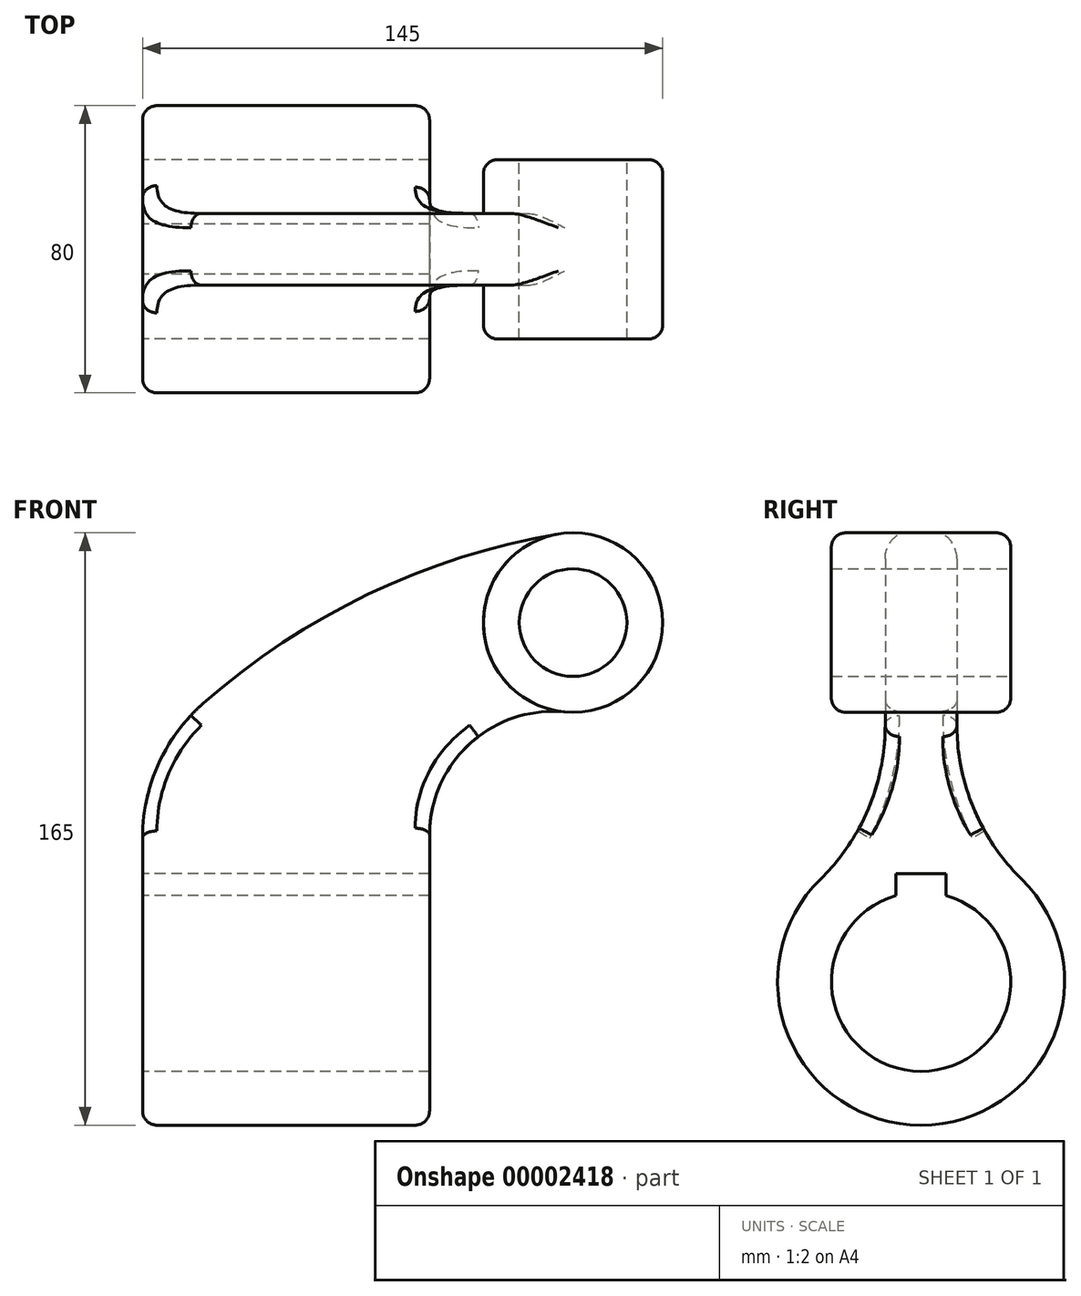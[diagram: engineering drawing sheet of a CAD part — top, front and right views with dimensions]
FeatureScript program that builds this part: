
annotation { "Feature Type Name" : "Feature", "Feature Type Description" : "" }
export const myFeature = defineFeature(function(context is Context, id is Id, definition is map)
    precondition{}
    {
        {
            var Q0;
            Q0=qCreatedBy(makeId("Front.planeOp"),FACE);
            var sketch = newSketch(context, id + "F0", { "sketchPlane" : qUnion([Q0])});
            skLineSegment(sketch, "E0", {"start": v(0, 0) * mm, "end": v(80, 0) * mm});
            skLineSegment(sketch, "E1", {"start": v(80, 0) * mm, "end": v(80, 40.8) * mm});
            skLineSegment(sketch, "E2", {"start": v(0, 0) * mm, "end": v(0, 40) * mm});
            skArc(sketch, "E3", {"start": v(0, 40) * mm, "mid": v(4.43, 60.58) * mm, "end": v(16.95, 77.52) * mm});
            skArc(sketch, "E4", {"start": v(16.95, 77.52) * mm, "mid": v(63.1, 107.99) * mm, "end": v(115.84, 124.65) * mm});
            skCircle(sketch, "E5", {"center": v(120, 100) * mm, "radius": 25 * mm});
            skArc(sketch, "E6", {"start": v(80, 40.8) * mm, "mid": v(91.26, 66.28) * mm, "end": v(117.67, 75.1) * mm});
            skCircle(sketch, "E7", {"center": v(120, 100) * mm, "radius": 15 * mm});
            skSolve(sketch);
        }
        {
            var Q0;
            Q0=qCreatedBy(makeId("Right.planeOp"),FACE);
            var sketch = newSketch(context, id + "F1", { "sketchPlane" : qUnion([Q0])});
            skCircle(sketch, "E8", {"center": v(0, 0) * mm, "radius": 40 * mm});
            skArc(sketch, "E9", {"start": v(-7, 24) * mm, "mid": v(0, -25) * mm, "end": v(7, 24) * mm});
            skLineSegment(sketch, "E10", {"start": v(0, 0) * mm, "end": v(0, -60.12) * mm, "construction": true});
            skLineSegment(sketch, "E11", {"start": v(0, 30) * mm, "end": v(7, 30) * mm});
            skLineSegment(sketch, "E12", {"start": v(7, 30) * mm, "end": v(7, 24) * mm});
            skLineSegment(sketch, "E13.0.MirrorCS", {"start": v(-7, 30) * mm, "end": v(-7, 24) * mm});
            skLineSegment(sketch, "E13.1.MirrorCS", {"start": v(0, 30) * mm, "end": v(-7, 30) * mm});
            skSolve(sketch);
        }
        {
            var Q0;
            Q0=makeQuery(id+"F1.imprint","IMPRINT",FACE,{"disambiguationData":[TD([[makeQuery(id+"F1.imprint","IMPRINT",EDGE,{"derivedFrom":sQuery(id+"F1.wireOp",EDGE,"E8")}),1.0]])]});
            var Q1;
            Q1=makeQuery(id+"F1.imprint","IMPRINT",FACE,{"disambiguationData":[TD([[makeQuery(id+"F1.imprint","IMPRINT",EDGE,{"derivedFrom":sQuery(id+"F1.wireOp",EDGE,"E9")}),1.0]])]});
            var Q2;
            Q2=sQuery(id+"F1.wireOp",EDGE,"E8");
            extrude(context, id + "F2", {"entities" : qUnion([Q0, Q1]), "surfaceEntities" : qUnion([Q2]), "depth" : 80 * mm});
        }
        {
            var Q0;
            Q0=makeQuery(id+"F0.imprint","IMPRINT",FACE,{"disambiguationData":[TD([[makeQuery(id+"F0.imprint","IMPRINT",EDGE,{"derivedFrom":sQuery(id+"F0.wireOp",EDGE,"E7")}),-1.0]])]});
            extrude(context, id + "F3", {"entities" : qUnion([Q0]), "endBound" : BoundingType.SYMMETRIC, "depth" : 50 * mm});
        }
        {
            var Q0;
            Q0=makeQuery(id+"F0.imprint","IMPRINT",FACE,{"disambiguationData":[TD([[makeQuery(id+"F0.imprint","IMPRINT",EDGE,{"derivedFrom":sQuery(id+"F0.wireOp",EDGE,"E0")}),1.0]])]});
            extrude(context, id + "F4", {"entities" : qUnion([Q0]), "endBound" : BoundingType.SYMMETRIC, "depth" : 20 * mm});
        }
        {
            var Q0;
            Q0=makeQuery(id+"F4.opExtrude","SWEPT_BODY",BODY,{"disambiguationData":[OSD([sQuery(id+"F0.wireOp",EDGE,"E0"),sQuery(id+"F0.wireOp",EDGE,"E1"),sQuery(id+"F0.wireOp",EDGE,"E2"),sQuery(id+"F0.wireOp",EDGE,"E3"),sQuery(id+"F0.wireOp",EDGE,"E4"),sQuery(id+"F0.wireOp",EDGE,"E5"),sQuery(id+"F0.wireOp",EDGE,"E6")])]});
            var Q1;
            Q1=makeQuery(id+"F2.opExtrude","SWEPT_BODY",BODY,{"disambiguationData":[OSD([sQuery(id+"F1.wireOp",EDGE,"E8")])]});
            var Q2;
            Q2=makeQuery(id+"F3.opExtrude","SWEPT_BODY",BODY,{"disambiguationData":[OSD([sQuery(id+"F0.wireOp",EDGE,"E5"),sQuery(id+"F0.wireOp",EDGE,"E7")])]});
            booleanBodies(context, id + "F5", {"operationType" : BooleanOperationType.UNION, "tools" : qUnion([Q0, Q1, Q2])});
        }
        {
            var Q0;
            Q0=makeQuery(id+"F1.imprint","IMPRINT",FACE,{"disambiguationData":[TD([[makeQuery(id+"F1.imprint","IMPRINT",EDGE,{"derivedFrom":sQuery(id+"F1.wireOp",EDGE,"E9")}),1.0]])]});
            extrude(context, id + "F6", {"entities" : qUnion([Q0]), "operationType" : NewBodyOperationType.REMOVE, "endBound" : BoundingType.THROUGH_ALL, "depth" : 25 * mm});
        }
        {
            var Q0;
            Q0=makeQuery(id+"F5.opBoolean","INTERSECT",EDGE,{"derivedFrom":[makeQuery(id+"F2.opExtrude","SWEPT_FACE",FACE,{"disambiguationData":[OSD([sQuery(id+"F1.wireOp",EDGE,"E8")])]}),makeQuery(id+"F4.opExtrude","CAP_FACE",FACE,{"disambiguationData":[OSD([sQuery(id+"F0.wireOp",EDGE,"E0"),sQuery(id+"F0.wireOp",EDGE,"E1"),sQuery(id+"F0.wireOp",EDGE,"E2"),sQuery(id+"F0.wireOp",EDGE,"E3"),sQuery(id+"F0.wireOp",EDGE,"E4"),sQuery(id+"F0.wireOp",EDGE,"E5"),sQuery(id+"F0.wireOp",EDGE,"E6")])],"isStart":false})]});
            var Q1;
            Q1=makeQuery(id+"F5.opBoolean","INTERSECT",EDGE,{"derivedFrom":[makeQuery(id+"F2.opExtrude","SWEPT_FACE",FACE,{"disambiguationData":[OSD([sQuery(id+"F1.wireOp",EDGE,"E8")])]}),makeQuery(id+"F4.opExtrude","CAP_FACE",FACE,{"disambiguationData":[OSD([sQuery(id+"F0.wireOp",EDGE,"E0"),sQuery(id+"F0.wireOp",EDGE,"E1"),sQuery(id+"F0.wireOp",EDGE,"E2"),sQuery(id+"F0.wireOp",EDGE,"E3"),sQuery(id+"F0.wireOp",EDGE,"E4"),sQuery(id+"F0.wireOp",EDGE,"E5"),sQuery(id+"F0.wireOp",EDGE,"E6")])],"isStart":true})]});
            fillet(context, id + "F7", {"entities" : qUnion([Q0, Q1]), "radius" : 60 * mm, "tangentPropagation" : true, "allowEdgeOverflow" : false});
        }
        {
            var Q0;
            Q0=makeQuery(id+"F4.opExtrude","CAP_EDGE",EDGE,{"disambiguationData":[OSD([sQuery(id+"F0.wireOp",EDGE,"E5")])],"isStart":false});
            var Q1;
            Q1=makeQuery(id+"F4.opExtrude","CAP_EDGE",EDGE,{"disambiguationData":[OSD([sQuery(id+"F0.wireOp",EDGE,"E5")])],"isStart":true});
            var Q2;
            Q2=makeQuery(id+"F3.opExtrude","CAP_EDGE",EDGE,{"disambiguationData":[OSD([sQuery(id+"F0.wireOp",EDGE,"E5")])],"isStart":true});
            var Q3;
            Q3=makeQuery(id+"F3.opExtrude","CAP_EDGE",EDGE,{"disambiguationData":[OSD([sQuery(id+"F0.wireOp",EDGE,"E5")])],"isStart":false});
            var Q4;
            Q4=makeQuery(id+"F2.opExtrude","CAP_EDGE",EDGE,{"disambiguationData":[OSD([sQuery(id+"F1.wireOp",EDGE,"E8")])],"isStart":false});
            var Q5;
            {var subQ0=sQuery(id+"F0.wireOp",EDGE,"E3");Q5=makeQuery(id+"F7.opFillet","BLEND_EDGE",EDGE,{"blendedFrom":[makeQuery(id+"F5.opBoolean","INTERSECT",EDGE,{"derivedFrom":[makeQuery(id+"F2.opExtrude","SWEPT_FACE",FACE,{"disambiguationData":[OSD([sQuery(id+"F1.wireOp",EDGE,"E8")])]}),makeQuery(id+"F4.opExtrude","CAP_FACE",FACE,{"disambiguationData":[OSD([sQuery(id+"F0.wireOp",EDGE,"E0"),sQuery(id+"F0.wireOp",EDGE,"E1"),sQuery(id+"F0.wireOp",EDGE,"E2"),subQ0,sQuery(id+"F0.wireOp",EDGE,"E4"),sQuery(id+"F0.wireOp",EDGE,"E5"),sQuery(id+"F0.wireOp",EDGE,"E6")])],"isStart":true})]}),makeQuery(id+"F4.opExtrude","SWEPT_FACE",FACE,{"disambiguationData":[OSD([subQ0])]})],"blendedInto":[makeQuery(id+"F4.opExtrude","SWEPT_FACE",FACE,{"disambiguationData":[OSD([subQ0])]})]});}
            fillet(context, id + "F8", {"entities" : qUnion([Q0, Q1, Q2, Q3, Q4, Q5]), "radius" : 4 * mm, "tangentPropagation" : true, "allowEdgeOverflow" : false});
        }
    });
